FCSTD DOCUMENT  (FreeCAD 0.19R24267 +99 (Git))
Label: test
License: All rights reserved
LicenseURL: http://en.wikipedia.org/wiki/All_rights_reserved
objects: Sketcher::SketchObject×1, PartDesign::Body×1
note: 2 computed .brp shape members not serialized (recipe doc carries the construction recipe); baked Part::Feature solids carry a one-line shape summary decoded from their .brp

FEATURE [Sketcher::SketchObject] Sketch
  FullyConstrained = false
  MapMode = 5
  Support = -> [XY_Plane]
  sketch-geometry (58):
    g0: LineSegment StartX=0 StartY=0 StartZ=0 EndX=44.62 EndY=0 EndZ=0
    g1: LineSegment StartX=44.62 StartY=0 StartZ=0 EndX=44.62 EndY=29.5903 EndZ=0
    g2: LineSegment StartX=44.62 StartY=29.5903 StartZ=0 EndX=0 EndY=29.5903 EndZ=0
    g3: LineSegment StartX=0 StartY=29.5903 StartZ=0 EndX=0 EndY=0 EndZ=0
    g4: Circle CenterX=4.90637 CenterY=30.9049 CenterZ=0 NormalX=0 NormalY=0 NormalZ=1 AngleXU=0 Radius=1.58639
    g5: Circle CenterX=39.4735 CenterY=30.9049 CenterZ=0 NormalX=0 NormalY=0 NormalZ=1 AngleXU=0 Radius=1.58639
    g6: Circle CenterX=39.4735 CenterY=3.72775 CenterZ=0 NormalX=0 NormalY=0 NormalZ=1 AngleXU=0 Radius=1.58639
    g7: Circle CenterX=4.90637 CenterY=3.72775 CenterZ=0 NormalX=0 NormalY=0 NormalZ=1 AngleXU=0 Radius=1.58639
    g8: LineSegment StartX=-14.953 StartY=18.5903 StartZ=0 EndX=-14.953 EndY=22.5903 EndZ=0
    g9: LineSegment StartX=-14.953 StartY=22.5903 StartZ=0 EndX=-18.4171 EndY=24.5903 EndZ=0
    g10: LineSegment StartX=-18.4171 StartY=24.5903 StartZ=0 EndX=-21.8812 EndY=22.5903 EndZ=0
    g11: LineSegment StartX=-21.8812 StartY=22.5903 StartZ=0 EndX=-21.8812 EndY=18.5903 EndZ=0
    g12: LineSegment StartX=-21.8812 StartY=18.5903 StartZ=0 EndX=-18.4171 EndY=16.5903 EndZ=0
    g13: LineSegment StartX=-18.4171 StartY=16.5903 StartZ=0 EndX=-14.953 EndY=18.5903 EndZ=0
    g14: Circle CenterX=-18.4171 CenterY=20.5903 CenterZ=0 NormalX=0 NormalY=0 NormalZ=1 AngleXU=0 Radius=4
    g15: LineSegment StartX=-9.95296 StartY=9.93002 StartZ=0 EndX=-9.95296 EndY=13.93 EndZ=0
    g16: LineSegment StartX=-9.95296 StartY=13.93 StartZ=0 EndX=-13.4171 EndY=15.93 EndZ=0
    g17: LineSegment StartX=-13.4171 StartY=15.93 StartZ=0 EndX=-16.8812 EndY=13.93 EndZ=0
    g18: LineSegment StartX=-16.8812 StartY=13.93 StartZ=0 EndX=-16.8812 EndY=9.93002 EndZ=0
    g19: LineSegment StartX=-16.8812 StartY=9.93002 StartZ=0 EndX=-13.4171 EndY=7.93002 EndZ=0
    g20: LineSegment StartX=-13.4171 StartY=7.93002 StartZ=0 EndX=-9.95296 EndY=9.93002 EndZ=0
    g21: Circle CenterX=-13.4171 CenterY=11.93 CenterZ=0 NormalX=0 NormalY=0 NormalZ=1 AngleXU=0 Radius=4
    g22: LineSegment StartX=-19.953 StartY=9.93002 StartZ=0 EndX=-19.953 EndY=13.93 EndZ=0
    g23: LineSegment StartX=-19.953 StartY=13.93 StartZ=0 EndX=-23.4171 EndY=15.93 EndZ=0
    g24: LineSegment StartX=-23.4171 StartY=15.93 StartZ=0 EndX=-26.8812 EndY=13.93 EndZ=0
    g25: LineSegment StartX=-26.8812 StartY=13.93 StartZ=0 EndX=-26.8812 EndY=9.93002 EndZ=0
    g26: LineSegment StartX=-26.8812 StartY=9.93002 StartZ=0 EndX=-23.4171 EndY=7.93002 EndZ=0
    g27: LineSegment StartX=-23.4171 StartY=7.93002 StartZ=0 EndX=-19.953 EndY=9.93002 EndZ=0
    g28: Circle CenterX=-23.4171 CenterY=11.93 CenterZ=0 NormalX=0 NormalY=0 NormalZ=1 AngleXU=0 Radius=4
    g29: LineSegment StartX=-13.4171 StartY=11.93 StartZ=0 EndX=-18.4171 EndY=20.5903 EndZ=0
    g30: LineSegment StartX=-18.4171 StartY=20.5903 StartZ=0 EndX=-23.4171 EndY=11.93 EndZ=0
    g31: LineSegment StartX=-23.4171 StartY=11.93 StartZ=0 EndX=-13.4171 EndY=11.93 EndZ=0
    g32: Circle CenterX=-18.4171 CenterY=14.8168 CenterZ=0 NormalX=0 NormalY=0 NormalZ=1 AngleXU=0 Radius=5.7735
    g33: LineSegment StartX=-33.4979 StartY=28.1193 StartZ=0 EndX=-33.4979 EndY=32.1193 EndZ=0
    g34: LineSegment StartX=-33.4979 StartY=32.1193 StartZ=0 EndX=-36.962 EndY=34.1193 EndZ=0
    g35: LineSegment StartX=-36.962 StartY=34.1193 StartZ=0 EndX=-40.4261 EndY=32.1193 EndZ=0
    g36: LineSegment StartX=-40.4261 StartY=32.1193 StartZ=0 EndX=-40.4261 EndY=28.1193 EndZ=0
    g37: LineSegment StartX=-40.4261 StartY=28.1193 StartZ=0 EndX=-36.962 EndY=26.1193 EndZ=0
    g38: LineSegment StartX=-36.962 StartY=26.1193 StartZ=0 EndX=-33.4979 EndY=28.1193 EndZ=0
    g39: Circle CenterX=-36.962 CenterY=30.1193 CenterZ=0 NormalX=0 NormalY=0 NormalZ=1 AngleXU=0 Radius=4
    g40: LineSegment StartX=-28.4979 StartY=19.459 StartZ=0 EndX=-28.4979 EndY=23.459 EndZ=0
    g41: LineSegment StartX=-28.4979 StartY=23.459 StartZ=0 EndX=-31.962 EndY=25.459 EndZ=0
    g42: LineSegment StartX=-31.962 StartY=25.459 StartZ=0 EndX=-35.4261 EndY=23.459 EndZ=0
    g43: LineSegment StartX=-35.4261 StartY=23.459 StartZ=0 EndX=-35.4261 EndY=19.459 EndZ=0
    g44: LineSegment StartX=-35.4261 StartY=19.459 StartZ=0 EndX=-31.962 EndY=17.459 EndZ=0
    g45: LineSegment StartX=-31.962 StartY=17.459 StartZ=0 EndX=-28.4979 EndY=19.459 EndZ=0
    g46: Circle CenterX=-31.962 CenterY=21.459 CenterZ=0 NormalX=0 NormalY=0 NormalZ=1 AngleXU=0 Radius=4
    g47: LineSegment StartX=-38.4979 StartY=19.459 StartZ=0 EndX=-38.4979 EndY=23.459 EndZ=0
    g48: LineSegment StartX=-38.4979 StartY=23.459 StartZ=0 EndX=-41.962 EndY=25.459 EndZ=0
    g49: LineSegment StartX=-41.962 StartY=25.459 StartZ=0 EndX=-45.4261 EndY=23.459 EndZ=0
    g50: LineSegment StartX=-45.4261 StartY=23.459 StartZ=0 EndX=-45.4261 EndY=19.459 EndZ=0
    g51: LineSegment StartX=-45.4261 StartY=19.459 StartZ=0 EndX=-41.962 EndY=17.459 EndZ=0
    g52: LineSegment StartX=-41.962 StartY=17.459 StartZ=0 EndX=-38.4979 EndY=19.459 EndZ=0
    g53: Circle CenterX=-41.962 CenterY=21.459 CenterZ=0 NormalX=0 NormalY=0 NormalZ=1 AngleXU=0 Radius=4
    g54: LineSegment StartX=-31.962 StartY=21.459 StartZ=0 EndX=-36.962 EndY=30.1193 EndZ=0
    g55: LineSegment StartX=-36.962 StartY=30.1193 StartZ=0 EndX=-41.962 EndY=21.459 EndZ=0
    g56: LineSegment StartX=-41.962 StartY=21.459 StartZ=0 EndX=-31.962 EndY=21.459 EndZ=0
    g57: Circle CenterX=-36.962 CenterY=24.3458 CenterZ=0 NormalX=0 NormalY=0 NormalZ=1 AngleXU=0 Radius=5.7735
  constraints (133):
    c: Coincident(g0,g1)
    c: Coincident(g1,g2)
    c: Coincident(g2,g3)
    c: Coincident(g3,g0)
    c: Horizontal(g0)
    c: Horizontal(g2)
    c: Vertical(g1)
    c: Vertical(g3)
    c: Coincident(g0,g-1)
    c: Distance(g2) = 44.62
    c: Horizontal(g4,g5)
    c: Vertical(g4,g7)
    c: Horizontal(g7,g6)
    c: Vertical(g5,g6)
    c: Equal(g4,g5)
    c: Equal(g4,g7)
    c: Equal(g4,g6)
    c: Coincident(g8,g9)
    c: Coincident(g9,g10)
    c: Coincident(g10,g11)
    c: Coincident(g11,g12)
    c: Coincident(g12,g13)
    c: Coincident(g13,g8)
    c: Equal(g8, g9-g13) x5
    c: PointOnObject(g8,g14)
    c: PointOnObject(g9,g14)
    c: PointOnObject(g10,g14)
    c: PointOnObject(g11,g14)
    c: PointOnObject(g12,g14)
    c: PointOnObject(g13,g14)
    c: Vertical(g11)
    c: Coincident(g15,g16)
    c: Coincident(g16,g17)
    c: Coincident(g17,g18)
    c: Coincident(g18,g19)
    c: Coincident(g19,g20)
    c: Coincident(g20,g15)
    c: Equal(g15, g16-g20) x5
    c: PointOnObject(g15,g21)
    c: PointOnObject(g16,g21)
    c: PointOnObject(g17,g21)
    c: PointOnObject(g18,g21)
    c: PointOnObject(g19,g21)
    c: PointOnObject(g20,g21)
    c: Vertical(g18)
    c: Coincident(g22,g23)
    c: Coincident(g23,g24)
    c: Coincident(g24,g25)
    c: Coincident(g25,g26)
    c: Coincident(g26,g27)
    c: Coincident(g27,g22)
    c: Equal(g22, g23-g27) x5
    c: PointOnObject(g22,g28)
    c: PointOnObject(g23,g28)
    c: PointOnObject(g24,g28)
    c: PointOnObject(g25,g28)
    c: PointOnObject(g26,g28)
    c: PointOnObject(g27,g28)
    c: Vertical(g25)
    c: Equal(g8,g18)
    c: Equal(g8,g25)
    c: Coincident(g29,g30)
    c: Coincident(g30,g31)
    c: Coincident(g31,g29)
    c: Equal(g29,g30)
    c: Equal(g29,g31)
    c: PointOnObject(g29,g32)
    c: PointOnObject(g30,g32)
    c: PointOnObject(g31,g32)
    c: Horizontal(g31)
    c: Coincident(g29,g14)
    c: Coincident(g21,g29)
    c: Distance(g9) = 4
    c: Distance(g29) = 10
    c: Coincident(g28,g30)
    c: Coincident(g33,g34)
    c: Coincident(g34,g35)
    c: Coincident(g35,g36)
    c: Coincident(g36,g37)
    c: Coincident(g37,g38)
    c: Coincident(g38,g33)
    c: Equal(g33, g34-g38) x5
    c: PointOnObject(g33,g39)
    c: PointOnObject(g34,g39)
    c: PointOnObject(g35,g39)
    c: PointOnObject(g36,g39)
    c: PointOnObject(g37,g39)
    c: PointOnObject(g38,g39)
    c: Vertical(g36)
    c: Coincident(g40,g41)
    c: Coincident(g41,g42)
    c: Coincident(g42,g43)
    c: Coincident(g43,g44)
    c: Coincident(g44,g45)
    c: Coincident(g45,g40)
    c: Equal(g40, g41-g45) x5
    c: PointOnObject(g40,g46)
    c: PointOnObject(g41,g46)
    c: PointOnObject(g42,g46)
    c: PointOnObject(g43,g46)
    c: PointOnObject(g44,g46)
    c: PointOnObject(g45,g46)
    c: Vertical(g43)
    c: Coincident(g47,g48)
    c: Coincident(g48,g49)
    c: Coincident(g49,g50)
    c: Coincident(g50,g51)
    c: Coincident(g51,g52)
    c: Coincident(g52,g47)
    c: Equal(g47, g48-g52) x5
    c: PointOnObject(g47,g53)
    c: PointOnObject(g48,g53)
    c: PointOnObject(g49,g53)
    c: PointOnObject(g50,g53)
    c: PointOnObject(g51,g53)
    c: PointOnObject(g52,g53)
    c: Vertical(g50)
    c: Equal(g33,g43)
    c: Equal(g33,g50)
    c: Coincident(g54,g55)
    c: Coincident(g55,g56)
    c: Coincident(g56,g54)
    c: Equal(g54,g55)
    c: Equal(g54,g56)
    c: PointOnObject(g54,g57)
    c: PointOnObject(g55,g57)
    c: PointOnObject(g56,g57)
    c: Horizontal(g56)
    c: Coincident(g54,g39)
    c: Coincident(g46,g54)
    c: Equal(g9,g34) = 4
    c: Equal(g29,g54) = 10
    c: Coincident(g53,g55)
FEATURE [PartDesign::Body] Body
  Group = -> [Sketch]
  Origin = -> Origin
